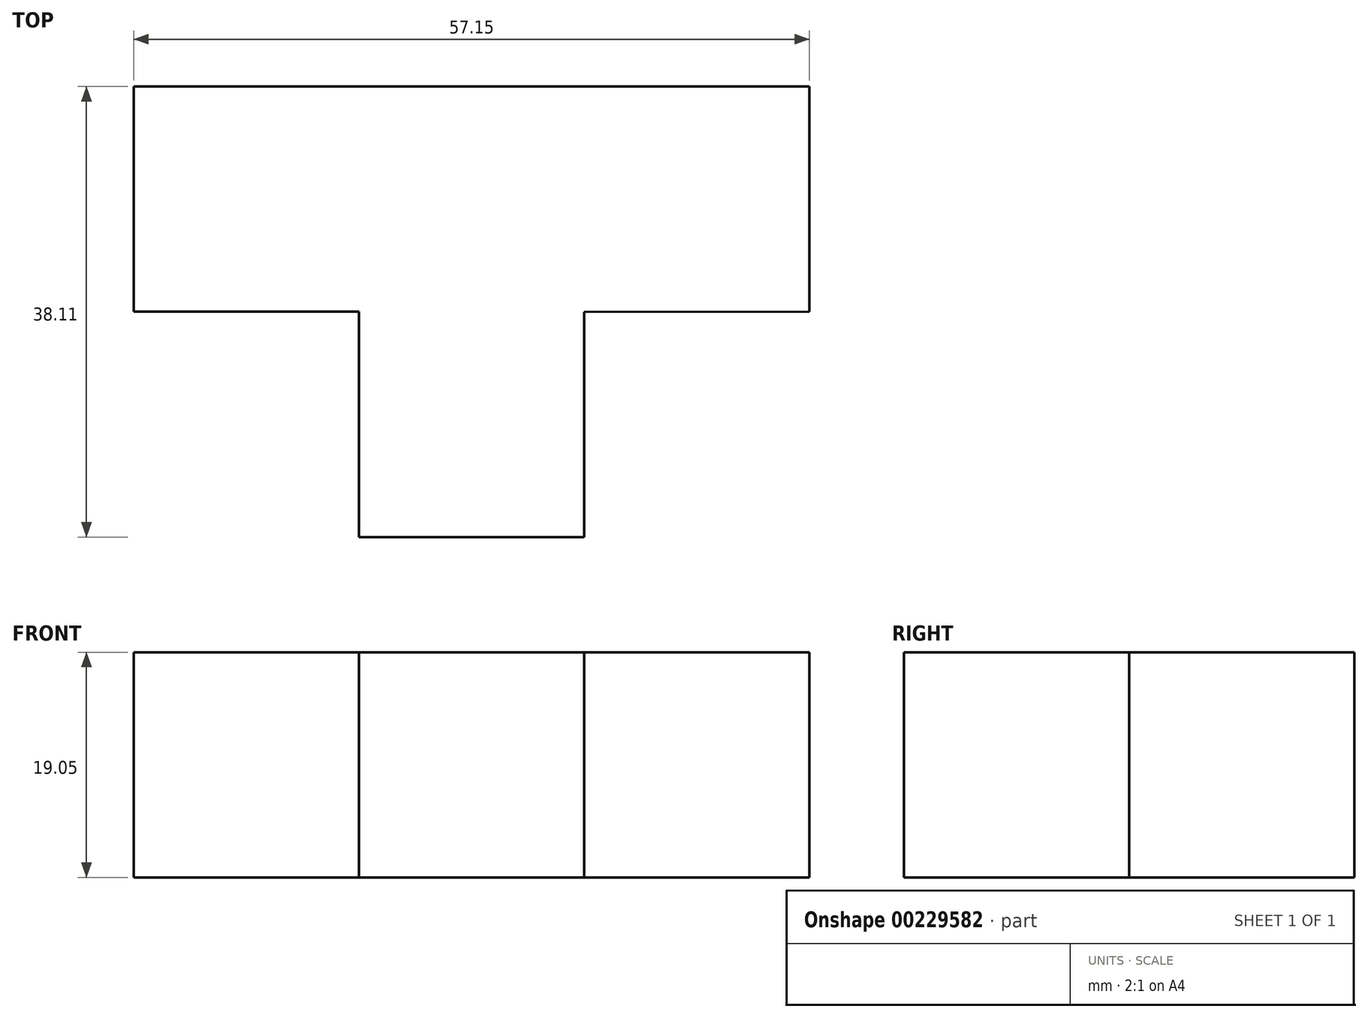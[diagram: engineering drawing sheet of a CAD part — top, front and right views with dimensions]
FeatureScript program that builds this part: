
annotation { "Feature Type Name" : "Feature", "Feature Type Description" : "" }
export const myFeature = defineFeature(function(context is Context, id is Id, definition is map)
    precondition{}
    {
        {
            var Q0;
            Q0=qCreatedBy(makeId("Top.planeOp"),FACE);
            var sketch = newSketch(context, id + "F0", { "sketchPlane" : qUnion([Q0])});
            skLineSegment(sketch, "E0", {"start": v(0, 0) * mm, "end": v(0, 19.06) * mm});
            skLineSegment(sketch, "E1", {"start": v(0, 0) * mm, "end": v(19.05, 0) * mm});
            skLineSegment(sketch, "E2", {"start": v(19.05, 0) * mm, "end": v(19.05, 19.05) * mm});
            skLineSegment(sketch, "E3", {"start": v(0, 19.06) * mm, "end": v(-19.05, 19.06) * mm});
            skLineSegment(sketch, "E4", {"start": v(19.05, 19.05) * mm, "end": v(38.1, 19.06) * mm});
            skPoint(sketch, "E4.endSnap0", {"position": v(-9.53, 19.06) * mm});
            skLineSegment(sketch, "E5", {"start": v(-19.05, 19.06) * mm, "end": v(-19.05, 38.11) * mm});
            skLineSegment(sketch, "E6", {"start": v(38.1, 19.06) * mm, "end": v(38.09, 38.11) * mm});
            skLineSegment(sketch, "E7", {"start": v(38.09, 38.11) * mm, "end": v(-19.05, 38.11) * mm});
            skSolve(sketch);
        }
        {
            var Q0;
            Q0 = qSketchRegion(id + "F0", true);
            extrude(context, id + "F1", {"entities" : qUnion([Q0]), "depth" : 19.05 * mm});
        }
    });
